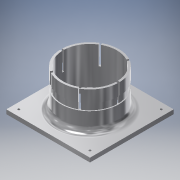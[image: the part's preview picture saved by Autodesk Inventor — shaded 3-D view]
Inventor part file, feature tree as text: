
AUTODESK INVENTOR PART (.ipt)
format: ipt  version: 2016 (Build 200138000, 138)  size: 209,408 bytes
history: native  units: mm
features: extrude x4, sketch x4, projected_geometry x2, plane x1, pattern_circular x1, fillet x1, reference x1
ambient origin geometry x8: Origin, YZ Plane, XZ Plane, XY Plane, X Axis, Y Axis, Z Axis, Center Point
bodies: Solid1 (feature_tree)
feature tree (14):
  extrude  "Extrusion1"  TaperAngle=0.0deg  [1 undecoded]
  extrude  "Extrusion2"  Depth=77.0mm
  plane  "Work Plane1"
  extrude  "Extrusion3"  Depth=54.0mm
  extrude  "Extrusion4"  [1 undecoded]
  pattern_circular  "Circular Pattern1"  [2 undecoded]
  fillet  "Fillet1"  Radius=10.0mm
  sketch  "Sketch1"  dims[d0=6.0mm d1=0.0mm]
  reference  "Reference1"
  sketch  "Sketch3"  dims[d3=75.0mm d4=77.0mm]
  sketch  "Sketch4"  dims[d5=3.0mm d6=54.0mm]
  sketch  "Sketch5"  dims[d7=0.0mm d8=-27.0mm d9=1.5mm d10=10.0mm d11=0.0mm d12=0.698132mm d13=0.0mm d14=0.0mm d15=60.0mm d16=360.0deg d18=9.0mm]
  projected_geometry  "Projected Loop1"
  projected_geometry  "Project Cut Edges1"
note: 4 required parameter values undecoded (feature->parameter linkage not recoverable at this tier; creation-order binding heuristic only, values carry confidence <= 0.55)
